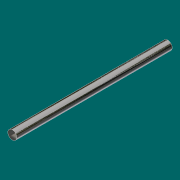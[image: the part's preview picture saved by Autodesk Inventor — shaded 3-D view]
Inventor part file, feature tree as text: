
AUTODESK INVENTOR PART (.ipt)
format: ipt  version: 2017 (Build 210142000, 142)  size: 71,680 bytes
history: native  units: in
note: dims shown in document units (in); Inventor stores cm internally (conversion verified against a paired STEP export)
features: extrude x1, sketch x1
ambient origin geometry x8: Origin, YZ Plane, XZ Plane, XY Plane, X Axis, Y Axis, Z Axis, Center Point
bodies: Solid1 (feature_tree)
feature tree (2):
  extrude  "Extrusion1"  Depth=39.0in TaperAngle=0.0deg
  sketch  "Sketch1"  dims[d0=2.25in d1=39.0in d2=0.0in]
